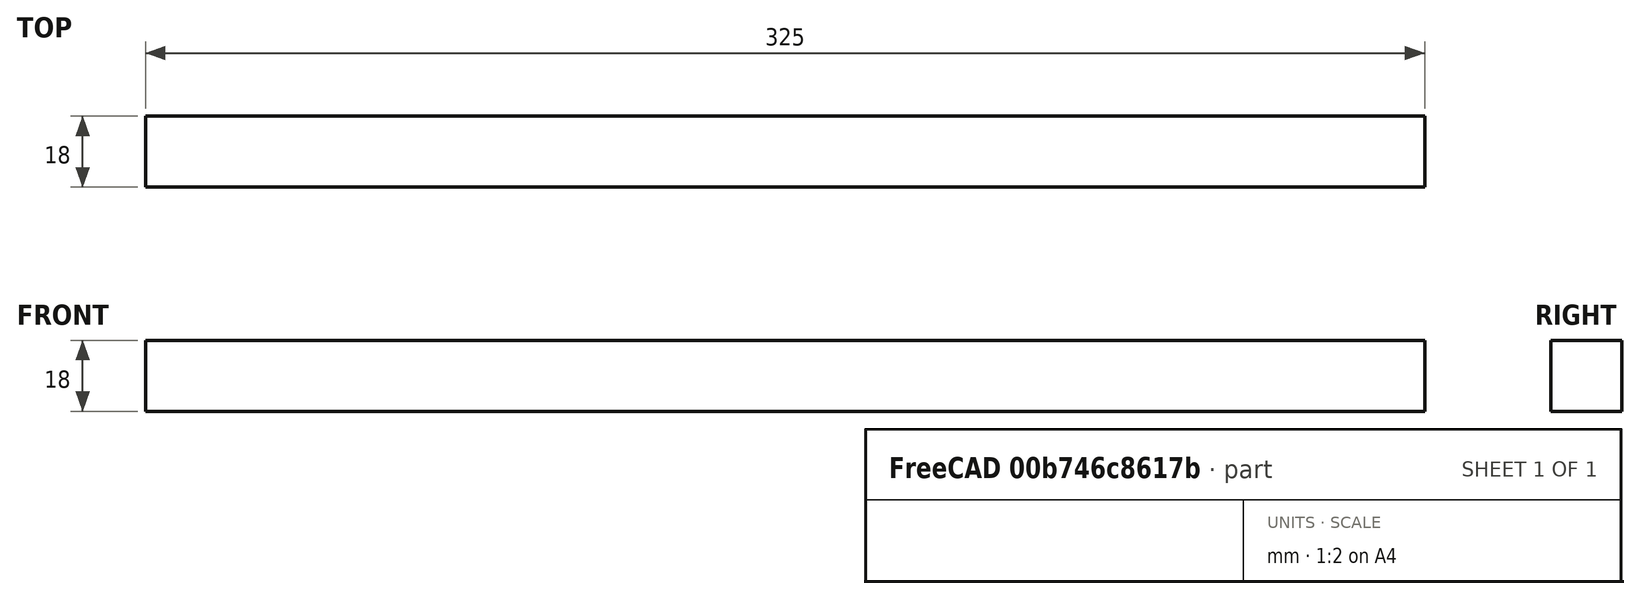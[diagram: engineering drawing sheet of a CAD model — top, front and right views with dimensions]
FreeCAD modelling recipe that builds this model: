
FCSTD DOCUMENT  (FreeCAD 0.19R24276 (Git))
Label: 3000_X_strut_x_18_18_325
License: All rights reserved
LicenseURL: http://en.wikipedia.org/wiki/All_rights_reserved
objects: Sketcher::SketchObject×1, PartDesign::Pad×1, PartDesign::Body×1
note: 4 computed .brp shape members not serialized (recipe doc carries the construction recipe); baked Part::Feature solids carry a one-line shape summary decoded from their .brp

FEATURE [Sketcher::SketchObject] Sketch
  FullyConstrained = true
  MapMode = 5
  Placement = pos=(0,0,0) rot=(0.57735,0.57735,0.57735;2.0944rad)
  Support = -> [YZ_Plane]
  sketch-geometry (4):
    g0: LineSegment StartX=0 StartY=0 StartZ=0 EndX=18 EndY=0 EndZ=0
    g1: LineSegment StartX=18 StartY=0 StartZ=0 EndX=18 EndY=18 EndZ=0
    g2: LineSegment StartX=18 StartY=18 StartZ=0 EndX=0 EndY=18 EndZ=0
    g3: LineSegment StartX=0 StartY=18 StartZ=0 EndX=0 EndY=0 EndZ=0
  constraints (11):
    c: Coincident(g0,g1)
    c: Coincident(g1,g2)
    c: Coincident(g2,g3)
    c: Coincident(g3,g0)
    c: Horizontal(g0)
    c: Horizontal(g2)
    c: Vertical(g1)
    c: Vertical(g3)
    c: Coincident(g0,g-1)
    c: DistanceX(g2,g2) = 18
    c: DistanceY(g1,g1) = 18
FEATURE [PartDesign::Pad] Pad
  Direction = (1,1,1)
  Length = 325
  Length2 = 100
  Placement = pos=(0,0,0) rot=(0.57735,0.57735,0.57735;2.0944rad)
  Profile = -> Sketch
  Type = 0
FEATURE [PartDesign::Body] Body
  Group = -> [Sketch,Pad]
  Origin = -> Origin
  Tip = -> Pad
